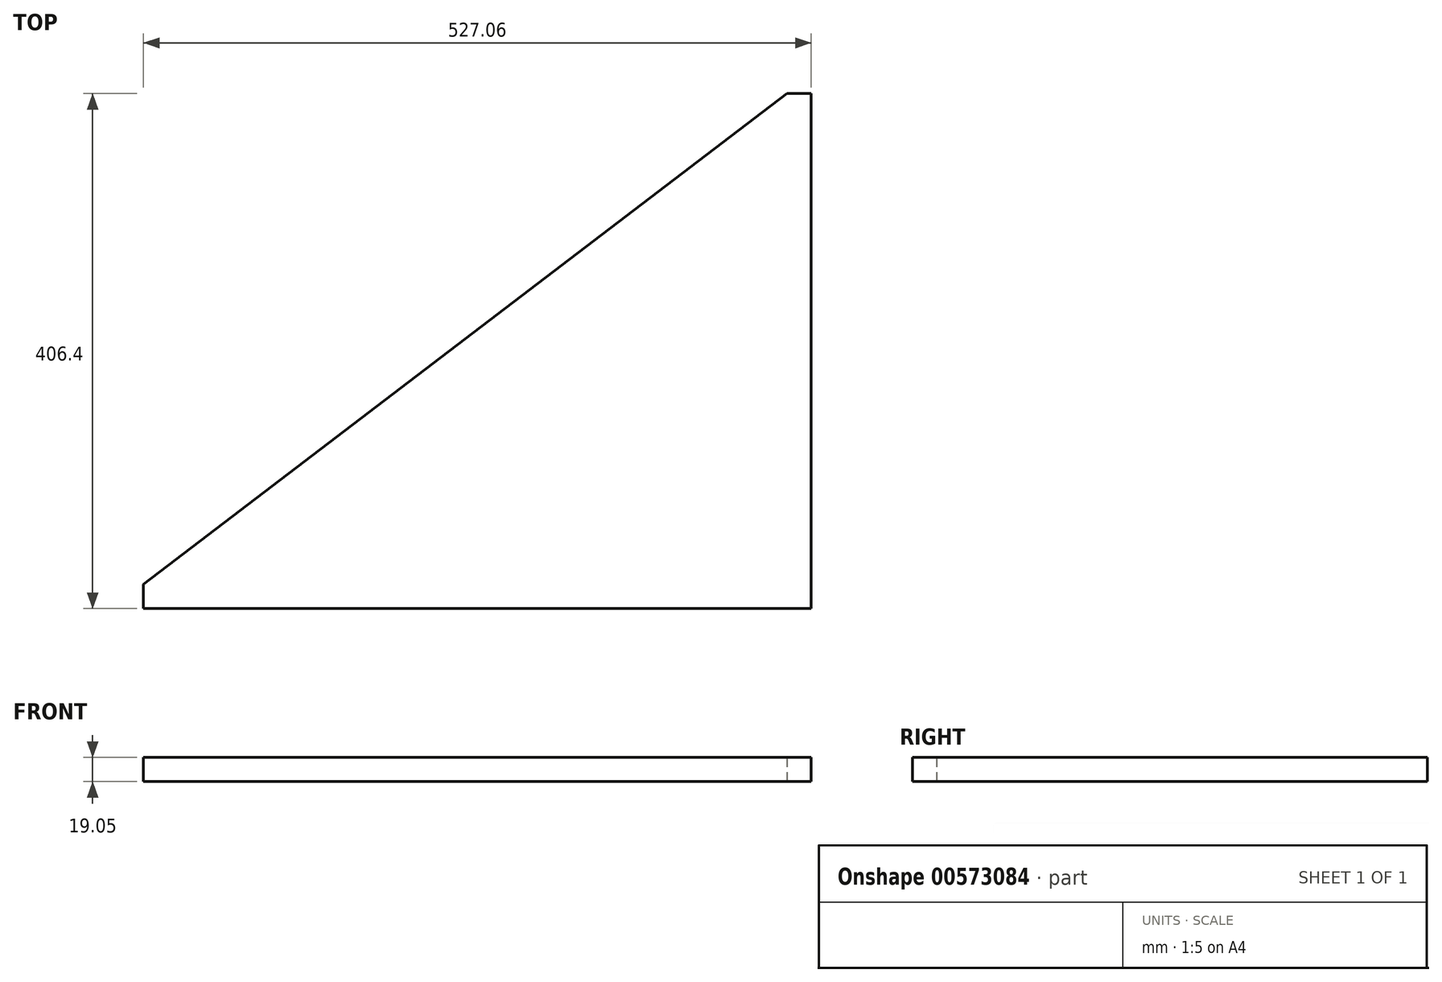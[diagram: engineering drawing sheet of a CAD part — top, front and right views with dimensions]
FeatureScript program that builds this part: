
annotation { "Feature Type Name" : "Feature", "Feature Type Description" : "" }
export const myFeature = defineFeature(function(context is Context, id is Id, definition is map)
    precondition{}
    {
        {
            var Q0;
            Q0=qCreatedBy(makeId("Top.planeOp"),FACE);
            var sketch = newSketch(context, id + "F0", { "sketchPlane" : qUnion([Q0])});
            skLineSegment(sketch, "E0.bottom", {"start": v(263.52, 203.2) * mm, "end": v(244.48, 203.2) * mm});
            skLineSegment(sketch, "E0.top", {"start": v(263.53, -203.2) * mm, "end": v(-263.53, -203.2) * mm});
            skLineSegment(sketch, "E0.left", {"start": v(263.52, 203.2) * mm, "end": v(263.53, -203.2) * mm});
            skLineSegment(sketch, "E0.right", {"start": v(-263.52, -184.15) * mm, "end": v(-263.52, -203.2) * mm});
            skPoint(sketch, "E0.middle", {"position": v(0, 0) * mm});
            skLineSegment(sketch, "E1", {"start": v(244.48, 203.2) * mm, "end": v(-263.53, -184.15) * mm});
            skPoint(sketch, "E2.orphan", {"position": v(-263.53, 203.2) * mm});
            skSolve(sketch);
        }
        {
            var Q0;
            Q0=makeQuery(id+"F0.imprint","IMPRINT",FACE,{"disambiguationData":[TD([[makeQuery(id+"F0.imprint","IMPRINT",EDGE,{"derivedFrom":sQuery(id+"F0.wireOp",EDGE,"E0.bottom")}),1.0]])]});
            extrude(context, id + "F1", {"entities" : qUnion([Q0]), "depth" : 19.05 * mm, "offsetDistance" : 25.4 * mm});
        }
    });
